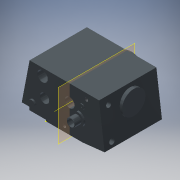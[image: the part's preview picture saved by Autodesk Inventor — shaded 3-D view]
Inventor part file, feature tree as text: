
AUTODESK INVENTOR PART (.ipt)
format: ipt  version: 2016 (Build 200138000, 138)  size: 363,008 bytes
history: native  units: in
note: dims shown in document units (in); Inventor stores cm internally (conversion verified against a paired STEP export)
features: sketch x21, extrude x19, fillet x2, thread x2, chamfer x1, hole x1, plane x1, other x1
ambient origin geometry x8: Origin, YZ Plane, XZ Plane, XY Plane, X Axis, Y Axis, Z Axis, Center Point
bodies: Solid1 (feature_tree)
feature tree (48):
  extrude  "Extrusion1"  Depth=10.4921in
  sketch  "Sketch3"  dims[d7=10.0in d8=0.5669in]
  extrude  "Extrusion2"  Depth=0.5669in
  extrude  "Extrusion3"  Depth=0.694in
  extrude  "Extrusion4"  Depth=0.7087in
  extrude  "Extrusion5"  Depth=0.0787in
  extrude  "Extrusion6"  Depth=13.4646in TaperAngle=0.0deg
  fillet  "Fillet1"  Radius=5.5118in
  fillet  "Fillet2"  Radius=6.2992in
  extrude  "Extrusion7"  Depth=2.7559in
  thread  "Thread1"  [1 undecoded]
  sketch  "Sketch9"  dims[d30=0.3937in d31=0.0in d34=1.1811in]
  extrude  "Extrusion8"  Depth=1.1811in
  extrude  "Extrusion9"  Depth=1.7717in
  extrude  "Extrusion10"  Depth=1.2106in
  chamfer  "Chamfer1"  Distance=2.3622in
  extrude  "Extrusion11"  Depth=0.748in
  extrude  "Extrusion12"  Depth=1.0236in TaperAngle=0.0deg
  extrude  "Extrusion13"  Depth=1.0236in TaperAngle=0.0deg
  extrude  "Extrusion14"  Depth=1.378in
  hole  "Hole1"  [1 undecoded]
  extrude  "Extrusion15"  Depth=0.0787in
  extrude  "Extrusion16"  Depth=0.7874in
  extrude  "Extrusion17"  Depth=0.3937in TaperAngle=0.0deg
  thread  "Thread2"  [1 undecoded]
  plane  "Work Plane2"
  extrude  "Extrusion18"  Depth=0.3937in TaperAngle=0.0deg
  extrude  "Extrusion19"  Depth=1.6929in
  sketch  "Sketch1"  dims[d0=8.6614in d1=10.4921in]
  sketch  "Sketch4"  dims[d9=9.6457in d10=0.694in]
  sketch  "Sketch5"  dims[d11=1.7717in d12=0.7087in]
  sketch  "Sketch6"  dims[d14=16.3386in d15=0.0787in]
  sketch  "Sketch7"  dims[d16=0.0787in d17=13.4646in d18=0.0in d22=5.5118in d26=6.2992in]
  sketch  "Sketch8"  dims[d27=2.7559in d28=3.6024in d29=2.7559in]
  sketch  "Sketch10"  dims[d37=1.7717in d38=2.0079in]
  sketch  "Sketch11"  dims[d39=1.2402in d42=1.2106in]
  sketch  "Sketch12"  dims[d43=1.8799in d44=2.3622in d45=0.0in]
  sketch  "Sketch13"  dims[d49=6.3386in d50=0.748in]
  sketch  "Sketch14"  dims[d52=7.4213in d53=1.0236in d54=0.0in]
  sketch  "Sketch15"  dims[d55=2.2835in d56=1.0236in d57=0.0in]
  sketch  "Sketch16"  dims[d69=0.7874in d70=1.378in]
  sketch  "Sketch17"  dims[d72=0.3937in d73=0.315in]
  sketch  "Sketch19"  dims[d75=0.2362in d76=0.0in d77=0.0787in]
  sketch  "Sketch20"  dims[d78=0.0787in d82=0.7874in]
  sketch  "Sketch21"  dims[d83=1.1811in d84=0.0in d85=0.3937in d86=0.0in d87=3.0118in]
  other  "Work Axis1"
  sketch  "Sketch22"  dims[d88=45.0deg d91=0.3937in d92=0.0in]
  sketch  "Sketch23"  dims[d93=2.0079in d94=1.6929in d95=1.4961in d96=0.0in d97=1.9685in d98=0.0in d99=0.0787in d100=0.0787in d101=45.0deg d103=1.1811in d105=0.3937in d106=0.0in d107=5.9055in d108=5.9646in d109=90.0deg d110=2.7559in d111=7.4803in d112=90.0deg d113=0.3937in d114=0.0in d116=0.3937in d117=0.0in d118=2.9528in d120=3.2283in d121=1.1811in d122=0.1969in d123=0.0in d124=0.2559in d125=0.1181in d126=0.2362in d127=0.2559in d128=0.0787in d129=90.0deg d130=0.1969in d131=0.0in d132=6.6929in d133=90.0deg d134=1.7323in d135=2.4409in d136=0.7874in d137=0.0in d138=5.9055in d139=5.9646in d140=90.0deg d141=2.1654in d142=2.7559in d143=0.0in d144=0.9843in d145=1.3386in d146=0.7874in d147=0.7874in d148=0.0in d149=0.3937in d150=0.0in d151=0.0in d152=1.2992in d153=0.0in d154=17.3258in d155=0.0in]
note: 3 required parameter values undecoded (feature->parameter linkage not recoverable at this tier; creation-order binding heuristic only, values carry confidence <= 0.55)
